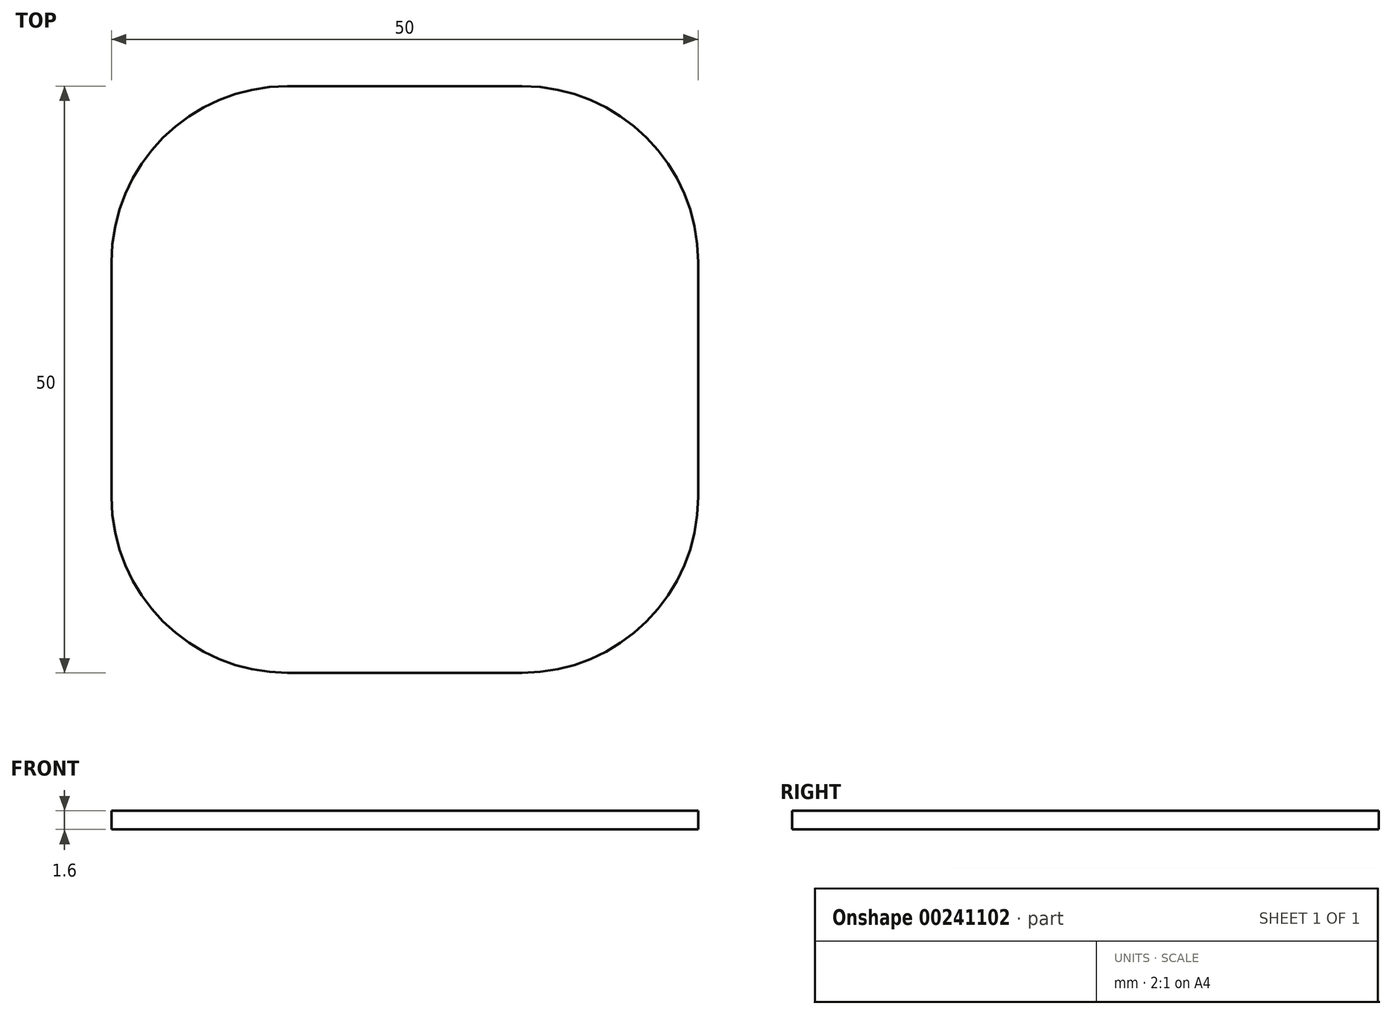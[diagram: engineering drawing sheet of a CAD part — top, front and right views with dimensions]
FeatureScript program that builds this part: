
annotation { "Feature Type Name" : "Feature", "Feature Type Description" : "" }
export const myFeature = defineFeature(function(context is Context, id is Id, definition is map)
    precondition{}
    {
        {
            var Q0;
            Q0=qCreatedBy(makeId("Top.planeOp"),FACE);
            var sketch = newSketch(context, id + "F0", { "sketchPlane" : qUnion([Q0])});
            skPoint(sketch, "E0.center", {"position": v(0, 0) * mm});
            skPoint(sketch, "E1.middle", {"position": v(0, 25.8) * mm});
            skLineSegment(sketch, "E2.bottom", {"start": v(10, -25) * mm, "end": v(-10, -25) * mm});
            skLineSegment(sketch, "E2.top", {"start": v(10, 25) * mm, "end": v(-10, 25) * mm});
            skLineSegment(sketch, "E2.left", {"start": v(25, -10) * mm, "end": v(25, 10) * mm});
            skLineSegment(sketch, "E2.right", {"start": v(-25, -10) * mm, "end": v(-25, 10) * mm});
            skArc(sketch, "E3.filletArc", {"start": v(-10, 25) * mm, "mid": v(-20.6, 20.6) * mm, "end": v(-25, 10) * mm});
            skArc(sketch, "E4.filletArc", {"start": v(25, 10) * mm, "mid": v(20.6, 20.6) * mm, "end": v(10, 25) * mm});
            skArc(sketch, "E5.filletArc", {"start": v(10, -25) * mm, "mid": v(20.6, -20.6) * mm, "end": v(25, -10) * mm});
            skArc(sketch, "E6.filletArc", {"start": v(-25, -10) * mm, "mid": v(-20.6, -20.6) * mm, "end": v(-10, -25) * mm});
            skSolve(sketch);
        }
        {
            var Q0;
            Q0=qSketchRegion(id+"F0",true);
            extrude(context, id + "F1", {"entities" : qUnion([Q0]), "depth" : 1.6 * mm});
        }
    });
